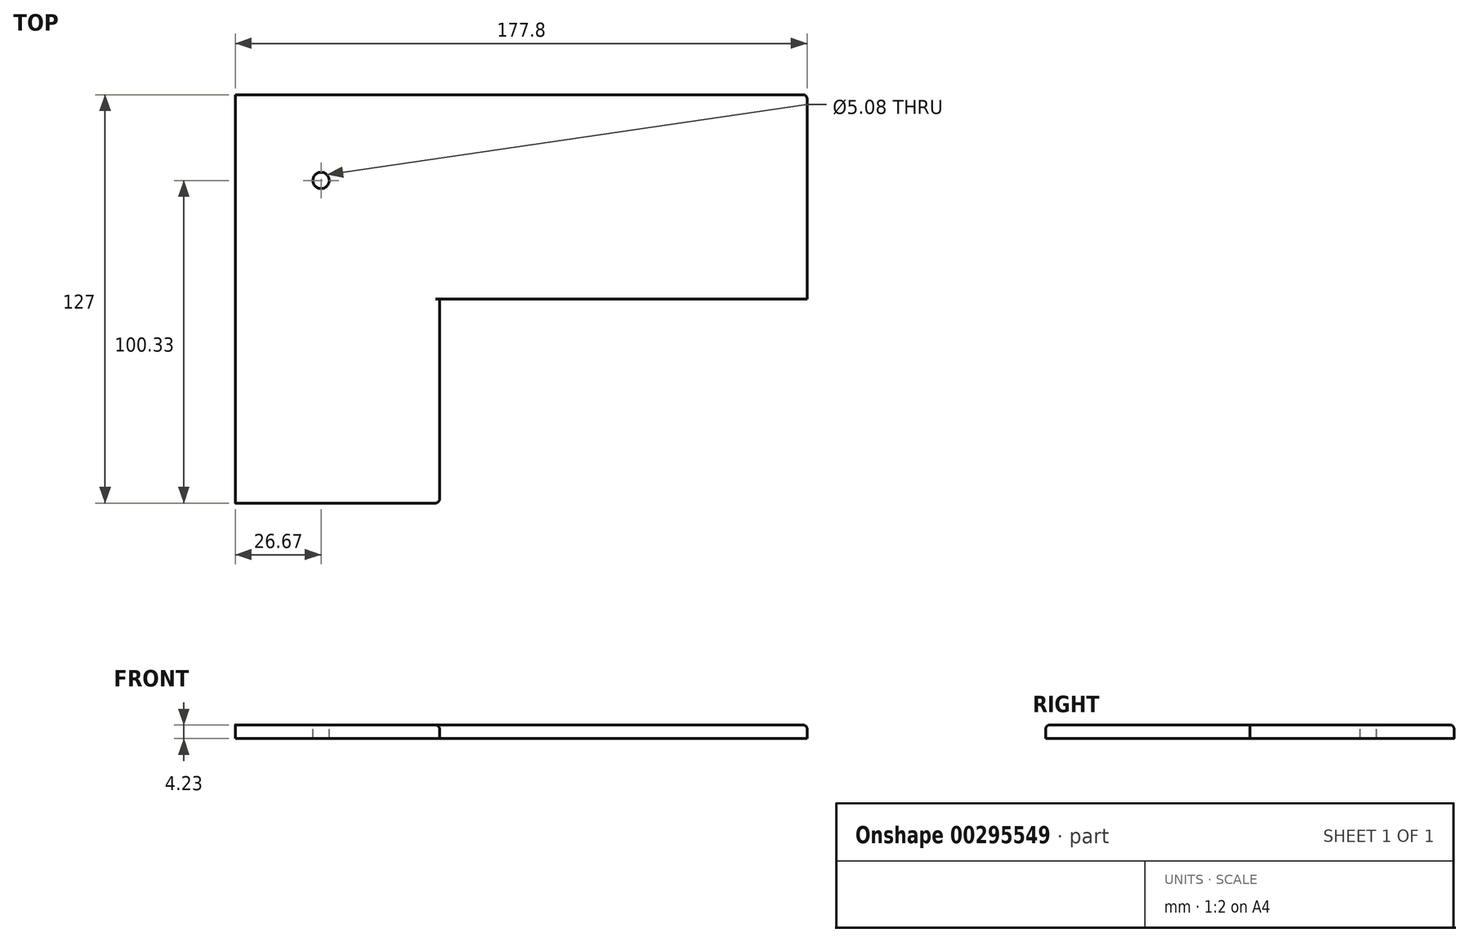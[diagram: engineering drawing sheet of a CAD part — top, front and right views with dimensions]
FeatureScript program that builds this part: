
annotation { "Feature Type Name" : "Feature", "Feature Type Description" : "" }
export const myFeature = defineFeature(function(context is Context, id is Id, definition is map)
    precondition{}
    {
        {
            var Q0;
            Q0=qCreatedBy(makeId("Top.planeOp"),FACE);
            var sketch = newSketch(context, id + "F0", { "sketchPlane" : qUnion([Q0])});
            skLineSegment(sketch, "E0.bottom", {"start": v(88.9, 31.75) * mm, "end": v(-88.9, 31.75) * mm});
            skLineSegment(sketch, "E0.top", {"start": v(88.9, -31.75) * mm, "end": v(-88.9, -31.75) * mm});
            skLineSegment(sketch, "E0.left", {"start": v(88.9, 31.75) * mm, "end": v(88.9, -31.75) * mm});
            skLineSegment(sketch, "E0.right", {"start": v(-88.9, 31.75) * mm, "end": v(-88.9, -31.75) * mm});
            skPoint(sketch, "E0.middle", {"position": v(0, 0) * mm});
            skLineSegment(sketch, "E1", {"start": v(88.9, -31.75) * mm, "end": v(-25.4, -31.75) * mm});
            skLineSegment(sketch, "E2", {"start": v(-25.4, -31.75) * mm, "end": v(-25.4, -95.25) * mm});
            skLineSegment(sketch, "E3", {"start": v(-88.9, -31.75) * mm, "end": v(-88.9, -95.25) * mm});
            skLineSegment(sketch, "E4", {"start": v(-88.9, 31.75) * mm, "end": v(-88.9, -95.25) * mm});
            skLineSegment(sketch, "E5", {"start": v(-88.9, -95.25) * mm, "end": v(-25.4, -95.25) * mm});
            skSolve(sketch);
        }
        {
            var Q0;
            Q0 = qSketchRegion(id + "F0", true);
            extrude(context, id + "F1", {"entities" : qUnion([Q0]), "depth" : 4.23 * mm});
        }
        {
            var Q0;
            Q0=makeQuery(id+"F1.opExtrude","CAP_EDGE",EDGE,{"disambiguationData":[OSD([sQuery(id+"F0.wireOp",EDGE,"E2")])],"isStart":false});
            var Q1;
            Q1=makeQuery(id+"F1.opExtrude","CAP_EDGE",EDGE,{"disambiguationData":[OSD([sQuery(id+"F0.wireOp",EDGE,"E5")])],"isStart":false});
            var Q2;
            Q2=makeQuery(id+"F1.opExtrude","CAP_EDGE",EDGE,{"disambiguationData":[OSD([sQuery(id+"F0.wireOp",EDGE,"E4")])],"isStart":false});
            var Q3;
            Q3=makeQuery(id+"F1.opExtrude","CAP_EDGE",EDGE,{"disambiguationData":[OSD([sQuery(id+"F0.wireOp",EDGE,"E0.bottom")])],"isStart":false});
            var Q4;
            Q4=makeQuery(id+"F1.opExtrude","CAP_EDGE",EDGE,{"disambiguationData":[OSD([sQuery(id+"F0.wireOp",EDGE,"E0.left")])],"isStart":false});
            var Q5;
            Q5=makeQuery(id+"F1.opExtrude","CAP_EDGE",EDGE,{"disambiguationData":[OSD([sQuery(id+"F0.wireOp",EDGE,"E1")])],"isStart":false});
            fillet(context, id + "F2", {"entities" : qUnion([Q0, Q1, Q2, Q3, Q4, Q5]), "radius" : 1.27 * mm, "tangentPropagation" : true, "allowEdgeOverflow" : false});
        }
        {
            var Q0;
            Q0=makeQuery(id+"F2.opFillet","BLEND_EDGE",EDGE,{"blendedFrom":[makeQuery(id+"F1.opExtrude","CAP_EDGE",EDGE,{"disambiguationData":[OSD([sQuery(id+"F0.wireOp",EDGE,"E2")])],"isStart":false}),makeQuery(id+"F1.opExtrude","CAP_EDGE",EDGE,{"disambiguationData":[OSD([sQuery(id+"F0.wireOp",EDGE,"E5")])],"isStart":false})],"blendedInto":[]});
            var Q1;
            Q1=makeQuery(id+"F1.opExtrude","SWEPT_EDGE",EDGE,{"disambiguationData":[OSD([sQuery(id+"F0.wireOp",EDGE,"E2"),sQuery(id+"F0.wireOp",EDGE,"E5")])]});
            var Q2;
            Q2=makeQuery(id+"F2.opFillet","BLEND_EDGE",EDGE,{"blendedFrom":[makeQuery(id+"F1.opExtrude","CAP_EDGE",EDGE,{"disambiguationData":[OSD([sQuery(id+"F0.wireOp",EDGE,"E4")])],"isStart":false}),makeQuery(id+"F1.opExtrude","CAP_EDGE",EDGE,{"disambiguationData":[OSD([sQuery(id+"F0.wireOp",EDGE,"E5")])],"isStart":false})],"blendedInto":[]});
            var Q3;
            Q3=makeQuery(id+"F2.opFillet","BLEND_EDGE",EDGE,{"blendedFrom":[makeQuery(id+"F1.opExtrude","CAP_EDGE",EDGE,{"disambiguationData":[OSD([sQuery(id+"F0.wireOp",EDGE,"E0.bottom")])],"isStart":false}),makeQuery(id+"F1.opExtrude","CAP_EDGE",EDGE,{"disambiguationData":[OSD([sQuery(id+"F0.wireOp",EDGE,"E0.left")])],"isStart":false})],"blendedInto":[]});
            var Q4;
            Q4=makeQuery(id+"F2.opFillet","BLEND_EDGE",EDGE,{"blendedFrom":[makeQuery(id+"F1.opExtrude","CAP_EDGE",EDGE,{"disambiguationData":[OSD([sQuery(id+"F0.wireOp",EDGE,"E0.left")])],"isStart":false}),makeQuery(id+"F1.opExtrude","CAP_EDGE",EDGE,{"disambiguationData":[OSD([sQuery(id+"F0.wireOp",EDGE,"E1")])],"isStart":false})],"blendedInto":[]});
            var Q5;
            Q5=makeQuery(id+"F2.opFillet","BLEND_EDGE",EDGE,{"blendedFrom":[makeQuery(id+"F1.opExtrude","CAP_EDGE",EDGE,{"disambiguationData":[OSD([sQuery(id+"F0.wireOp",EDGE,"E1")])],"isStart":false}),makeQuery(id+"F1.opExtrude","CAP_EDGE",EDGE,{"disambiguationData":[OSD([sQuery(id+"F0.wireOp",EDGE,"E2")])],"isStart":false})],"blendedInto":[]});
            var Q6;
            Q6=makeQuery(id+"F2.opFillet","BLEND_EDGE",EDGE,{"blendedFrom":[makeQuery(id+"F1.opExtrude","CAP_EDGE",EDGE,{"disambiguationData":[OSD([sQuery(id+"F0.wireOp",EDGE,"E0.bottom")])],"isStart":false}),makeQuery(id+"F1.opExtrude","CAP_EDGE",EDGE,{"disambiguationData":[OSD([sQuery(id+"F0.wireOp",EDGE,"E4")])],"isStart":false})],"blendedInto":[]});
            fillet(context, id + "F3", {"entities" : qUnion([Q0, Q1, Q2, Q3, Q4, Q5, Q6]), "radius" : 1.27 * mm, "tangentPropagation" : true, "allowEdgeOverflow" : false});
        }
        {
            var Q0;
            Q0=makeQuery(id+"F1.opExtrude","CAP_FACE",FACE,{"disambiguationData":[OSD([sQuery(id+"F0.wireOp",EDGE,"E0.bottom"),sQuery(id+"F0.wireOp",EDGE,"E0.left"),sQuery(id+"F0.wireOp",EDGE,"E1"),sQuery(id+"F0.wireOp",EDGE,"E2"),sQuery(id+"F0.wireOp",EDGE,"E4"),sQuery(id+"F0.wireOp",EDGE,"E5")])],"isStart":false});
            var sketch = newSketch(context, id + "F4", { "sketchPlane" : qUnion([Q0])});
            skLineSegment(sketch, "E6", {"start": v(-87.63, 30.48) * mm, "end": v(-62.23, 30.48) * mm});
            skLineSegment(sketch, "E7", {"start": v(-62.23, 30.48) * mm, "end": v(-62.23, 5.08) * mm});
            skCircle(sketch, "E8", {"center": v(-62.23, 5.08) * mm, "radius": 2.54 * mm});
            skSolve(sketch);
        }
        {
            var Q0;
            Q0 = qSketchRegion(id + "F4", true);
            extrude(context, id + "F5", {"entities" : qUnion([Q0]), "operationType" : NewBodyOperationType.REMOVE, "endBound" : BoundingType.THROUGH_ALL, "oppositeDirection" : true, "depth" : 25.4 * mm});
        }
    });
